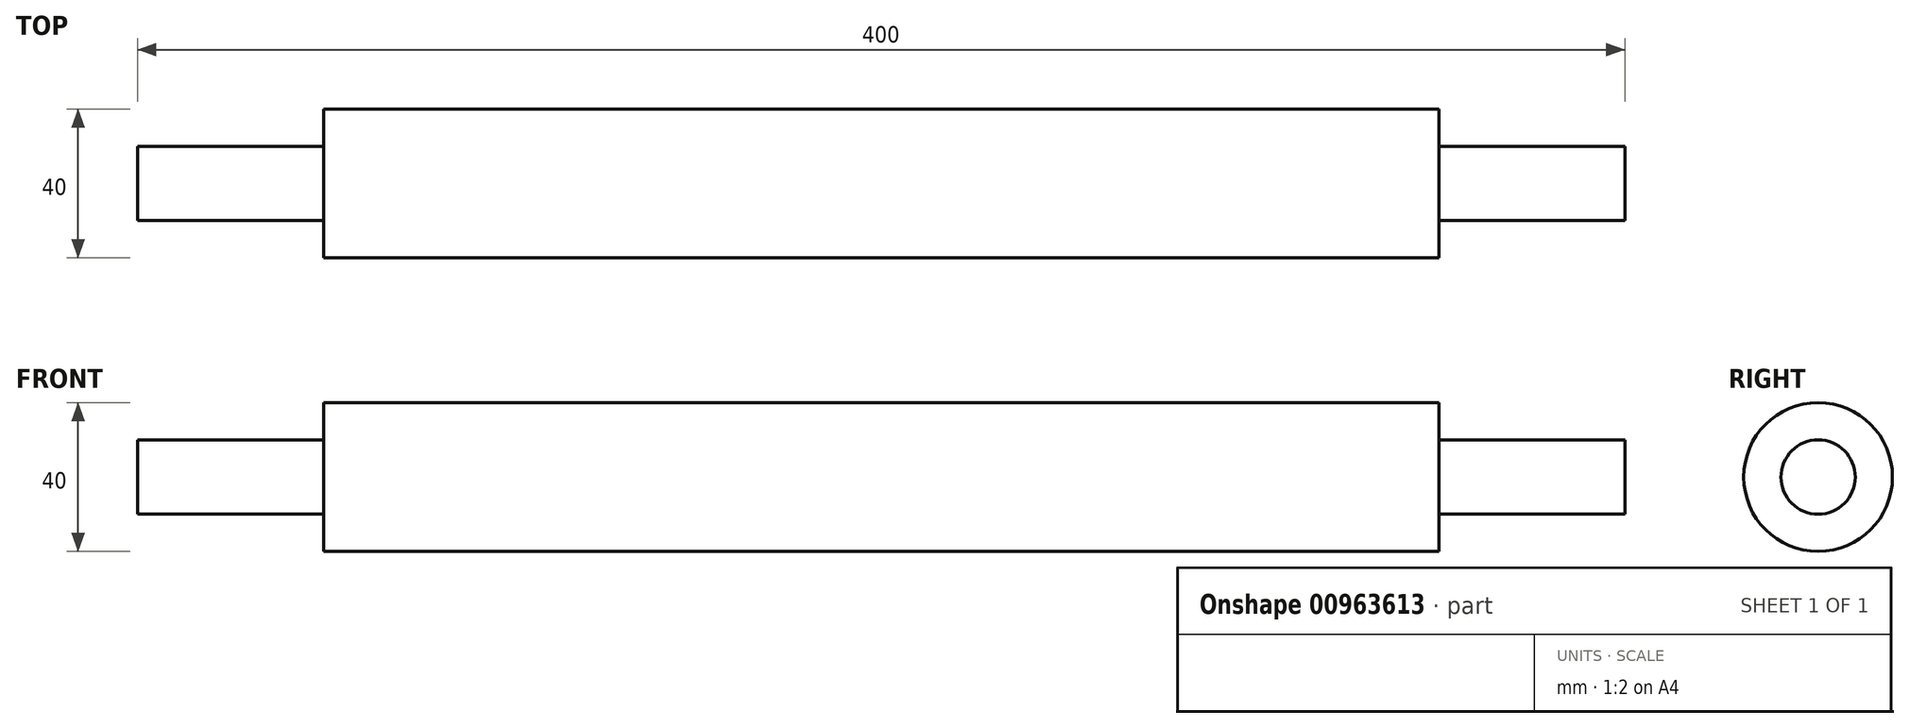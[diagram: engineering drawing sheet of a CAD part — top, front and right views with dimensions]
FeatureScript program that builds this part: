
annotation { "Feature Type Name" : "Feature", "Feature Type Description" : "" }
export const myFeature = defineFeature(function(context is Context, id is Id, definition is map)
    precondition{}
    {
        {
            var Q0;
            Q0=qCreatedBy(makeId("Right.planeOp"),FACE);
            var sketch = newSketch(context, id + "F0", { "sketchPlane" : qUnion([Q0])});
            skCircle(sketch, "E0", {"center": v(0, 0) * mm, "radius": 10 * mm});
            skSolve(sketch);
        }
        {
            var Q0;
            Q0 = qSketchRegion(id + "F0", true);
            extrude(context, id + "F1", {"entities" : qUnion([Q0]), "oppositeDirection" : true, "depth" : 400 * mm, "offsetDistance" : 25.4 * mm});
        }
        {
            var Q0;
            Q0=qCreatedBy(makeId("Right.planeOp"),FACE);
            cPlane(context, id + "F2", {"entities" : qUnion([Q0]), "cplaneType" : CPlaneType.OFFSET, "offset" : 200 * mm, "oppositeDirection" : true, "width" : 152.4 * mm, "height" : 152.4 * mm});
        }
        {
            var Q0;
            Q0=qCreatedBy(id+"F2.planeOp",FACE);
            var sketch = newSketch(context, id + "F3", { "sketchPlane" : qUnion([Q0])});
            skCircle(sketch, "E1", {"center": v(0, 0) * mm, "radius": 20 * mm});
            skSolve(sketch);
        }
        {
            var Q0;
            Q0 = qSketchRegion(id + "F3", true);
            extrude(context, id + "F4", {"entities" : qUnion([Q0]), "operationType" : NewBodyOperationType.ADD, "endBound" : BoundingType.SYMMETRIC, "depth" : 300 * mm, "offsetDistance" : 25.4 * mm});
        }
    });
